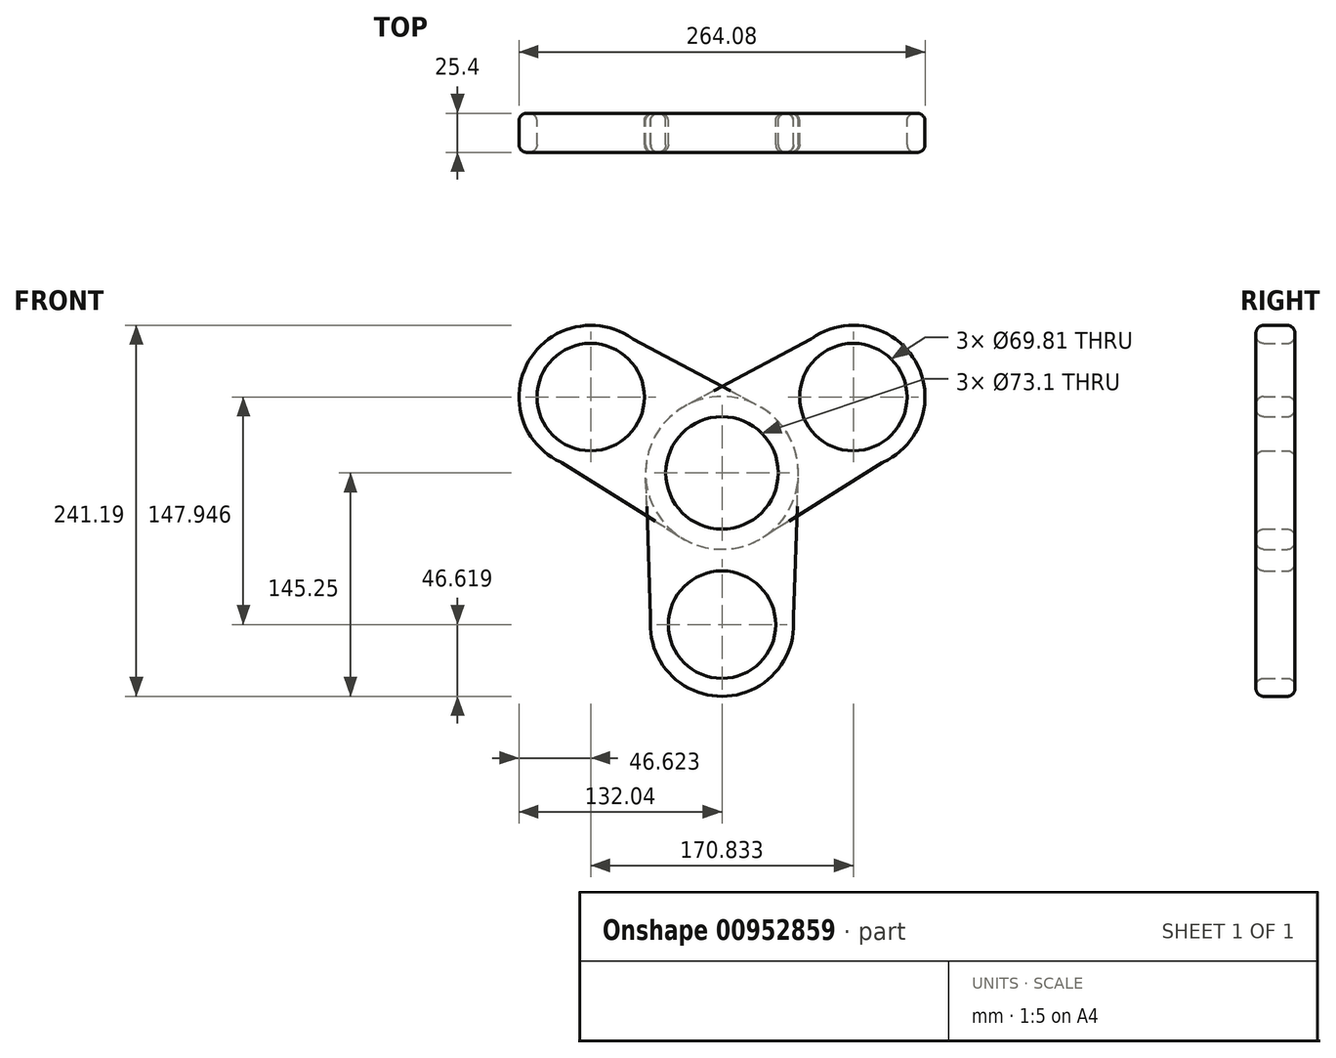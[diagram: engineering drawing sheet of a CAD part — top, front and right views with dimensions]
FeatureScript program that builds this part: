
annotation { "Feature Type Name" : "Feature", "Feature Type Description" : "" }
export const myFeature = defineFeature(function(context is Context, id is Id, definition is map)
    precondition{}
    {
        {
            var Q0;
            Q0=qCreatedBy(makeId("Front.planeOp"),FACE);
            var sketch = newSketch(context, id + "F0", { "sketchPlane" : qUnion([Q0])});
            skCircle(sketch, "E0", {"center": v(0, 0) * mm, "radius": 36.55 * mm});
            skCircle(sketch, "E1", {"center": v(0, 0) * mm, "radius": 49.65 * mm});
            skCircle(sketch, "E2", {"center": v(0, -98.63) * mm, "radius": 46.62 * mm});
            skLineSegment(sketch, "E3", {"start": v(46.38, -93.91) * mm, "end": v(49.68, 0) * mm});
            skLineSegment(sketch, "E4", {"start": v(-46.39, -93.95) * mm, "end": v(-49.68, 0) * mm});
            skCircle(sketch, "E5", {"center": v(0, -98.63) * mm, "radius": 34.9 * mm});
            skSolve(sketch);
        }
        {
            var Q0;
            Q0=makeQuery(id+"F0.imprint","IMPRINT",FACE,{"disambiguationData":[TD([[makeQuery(id+"F0.imprint","IMPRINT",EDGE,{"derivedFrom":sQuery(id+"F0.wireOp",EDGE,"E5")}),-1.0]])]});
            var Q1;
            Q1=makeQuery(id+"F0.imprint","IMPRINT",FACE,{"disambiguationData":[TD([[makeQuery(id+"F0.imprint","IMPRINT",EDGE,{"derivedFrom":sQuery(id+"F0.wireOp",EDGE,"E0")}),-1.0]])]});
            var Q2;
            {var subQ0=sQuery(id+"F0.wireOp",EDGE,"E3");var subQ1=sQuery(id+"F0.wireOp",EDGE,"E1");var subQ2=makeQuery(id+"F0.imprint","INTERSECT",VERTEX,{"derivedFrom":[subQ1,subQ0]});Q2=makeQuery(id+"F0.imprint","IMPRINT",FACE,{"disambiguationData":[TD([[makeQuery(id+"F0.imprint","IMPRINT",EDGE,{"disambiguationData":[TD([[subQ2,1.0]])],"derivedFrom":subQ1}),-1.0]])]});}
            extrude(context, id + "F1", {"entities" : qUnion([Q0, Q1, Q2]), "depth" : 25.4 * mm, "offsetDistance" : 25.4 * mm});
        }
        {
            var Q0;
            Q0=makeQuery(id+"F1.opExtrude","SWEPT_BODY",BODY,{"disambiguationData":[OSD([sQuery(id+"F0.wireOp",EDGE,"E0"),sQuery(id+"F0.wireOp",EDGE,"E1"),sQuery(id+"F0.wireOp",EDGE,"E2"),sQuery(id+"F0.wireOp",EDGE,"E3"),sQuery(id+"F0.wireOp",EDGE,"E4"),sQuery(id+"F0.wireOp",EDGE,"E5")])]});
            var Q1;
            Q1=makeQuery(id+"F1.opExtrude","CAP_EDGE",EDGE,{"disambiguationData":[OSD([sQuery(id+"F0.wireOp",EDGE,"E0")])],"isStart":false});
            circularPattern(context, id + "F2", {"entities" : qUnion([Q0]), "axis" : qUnion([Q1]), "angle" : 360 * degree, "instanceCount" : 3, "equalSpace" : true});
        }
        {
            var Q0;
            Q0=makeQuery(id+"F2.opPattern","COPY",EDGE,{"derivedFrom":makeQuery(id+"F1.opExtrude","CAP_EDGE",EDGE,{"disambiguationData":[OSD([sQuery(id+"F0.wireOp",EDGE,"E5")])],"isStart":true}),"instanceName":"2"});
            var Q1;
            Q1=makeQuery(id+"F2.opPattern","COPY",EDGE,{"derivedFrom":makeQuery(id+"F1.opExtrude","CAP_EDGE",EDGE,{"disambiguationData":[OSD([sQuery(id+"F0.wireOp",EDGE,"E2")])],"isStart":true}),"instanceName":"2"});
            var Q2;
            Q2=makeQuery(id+"F2.opPattern","COPY",EDGE,{"derivedFrom":makeQuery(id+"F1.opExtrude","CAP_EDGE",EDGE,{"disambiguationData":[OSD([sQuery(id+"F0.wireOp",EDGE,"E2")])],"isStart":false}),"instanceName":"2"});
            var Q3;
            Q3=makeQuery(id+"F2.opPattern","COPY",EDGE,{"derivedFrom":makeQuery(id+"F1.opExtrude","CAP_EDGE",EDGE,{"disambiguationData":[OSD([sQuery(id+"F0.wireOp",EDGE,"E4")])],"isStart":true}),"instanceName":"2"});
            var Q4;
            Q4=makeQuery(id+"F2.opPattern","COPY",EDGE,{"derivedFrom":makeQuery(id+"F1.opExtrude","CAP_EDGE",EDGE,{"disambiguationData":[OSD([sQuery(id+"F0.wireOp",EDGE,"E5")])],"isStart":true}),"instanceName":"1"});
            var Q5;
            Q5=makeQuery(id+"F1.opExtrude","SWEPT_FACE",FACE,{"disambiguationData":[OSD([sQuery(id+"F0.wireOp",EDGE,"E5")])]});
            var Q6;
            Q6=makeQuery(id+"F2.opPattern","COPY",FACE,{"derivedFrom":makeQuery(id+"F1.opExtrude","SWEPT_FACE",FACE,{"disambiguationData":[OSD([sQuery(id+"F0.wireOp",EDGE,"E1")])]}),"instanceName":"1"});
            var Q7;
            Q7=makeQuery(id+"F2.opPattern","COPY",EDGE,{"derivedFrom":makeQuery(id+"F1.opExtrude","SWEPT_EDGE",EDGE,{"disambiguationData":[OSD([sQuery(id+"F0.wireOp",EDGE,"E1"),sQuery(id+"F0.wireOp",EDGE,"E3")])]}),"instanceName":"2"});
            var Q8;
            Q8=makeQuery(id+"F1.opExtrude","SWEPT_EDGE",EDGE,{"disambiguationData":[OSD([sQuery(id+"F0.wireOp",EDGE,"E1"),sQuery(id+"F0.wireOp",EDGE,"E4")])]});
            var Q9;
            Q9=makeQuery(id+"F2.opPattern","COPY",EDGE,{"derivedFrom":makeQuery(id+"F1.opExtrude","CAP_EDGE",EDGE,{"disambiguationData":[OSD([sQuery(id+"F0.wireOp",EDGE,"E0")])],"isStart":true}),"instanceName":"1"});
            var Q10;
            Q10=makeQuery(id+"F1.opExtrude","SWEPT_FACE",FACE,{"disambiguationData":[OSD([sQuery(id+"F0.wireOp",EDGE,"E1")])]});
            var Q11;
            Q11=makeQuery(id+"F1.opExtrude","SWEPT_EDGE",EDGE,{"disambiguationData":[OSD([sQuery(id+"F0.wireOp",EDGE,"E2"),sQuery(id+"F0.wireOp",EDGE,"E3")])]});
            var Q12;
            Q12=makeQuery(id+"F2.opPattern","COPY",EDGE,{"derivedFrom":makeQuery(id+"F1.opExtrude","SWEPT_EDGE",EDGE,{"disambiguationData":[OSD([sQuery(id+"F0.wireOp",EDGE,"E2"),sQuery(id+"F0.wireOp",EDGE,"E4")])]}),"instanceName":"1"});
            var Q13;
            Q13=makeQuery(id+"F2.opPattern","COPY",EDGE,{"derivedFrom":makeQuery(id+"F1.opExtrude","SWEPT_EDGE",EDGE,{"disambiguationData":[OSD([sQuery(id+"F0.wireOp",EDGE,"E1"),sQuery(id+"F0.wireOp",EDGE,"E3")])]}),"instanceName":"1"});
            var Q14;
            Q14=makeQuery(id+"F1.opExtrude","CAP_EDGE",EDGE,{"disambiguationData":[OSD([sQuery(id+"F0.wireOp",EDGE,"E0")])],"isStart":true});
            var Q15;
            Q15=makeQuery(id+"F1.opExtrude","CAP_EDGE",EDGE,{"disambiguationData":[OSD([sQuery(id+"F0.wireOp",EDGE,"E0")])],"isStart":false});
            var Q16;
            Q16=makeQuery(id+"F1.opExtrude","CAP_EDGE",EDGE,{"disambiguationData":[OSD([sQuery(id+"F0.wireOp",EDGE,"E3")])],"isStart":true});
            var Q17;
            Q17=makeQuery(id+"F2.opPattern","COPY",FACE,{"derivedFrom":makeQuery(id+"F1.opExtrude","SWEPT_FACE",FACE,{"disambiguationData":[OSD([sQuery(id+"F0.wireOp",EDGE,"E4")])]}),"instanceName":"1"});
            var Q18;
            Q18=makeQuery(id+"F2.opPattern","COPY",EDGE,{"derivedFrom":makeQuery(id+"F1.opExtrude","CAP_EDGE",EDGE,{"disambiguationData":[OSD([sQuery(id+"F0.wireOp",EDGE,"E3")])],"isStart":true}),"instanceName":"1"});
            var Q19;
            Q19=makeQuery(id+"F1.opExtrude","CAP_EDGE",EDGE,{"disambiguationData":[OSD([sQuery(id+"F0.wireOp",EDGE,"E1")])],"isStart":false});
            var Q20;
            Q20=makeQuery(id+"F1.opExtrude","CAP_EDGE",EDGE,{"disambiguationData":[OSD([sQuery(id+"F0.wireOp",EDGE,"E2")])],"isStart":false});
            var Q21;
            Q21=makeQuery(id+"F2.opPattern","COPY",FACE,{"derivedFrom":makeQuery(id+"F1.opExtrude","CAP_FACE",FACE,{"disambiguationData":[OSD([sQuery(id+"F0.wireOp",EDGE,"E0"),sQuery(id+"F0.wireOp",EDGE,"E1"),sQuery(id+"F0.wireOp",EDGE,"E2"),sQuery(id+"F0.wireOp",EDGE,"E3"),sQuery(id+"F0.wireOp",EDGE,"E4"),sQuery(id+"F0.wireOp",EDGE,"E5")])],"isStart":true}),"instanceName":"1"});
            var Q22;
            Q22=makeQuery(id+"F1.opExtrude","CAP_FACE",FACE,{"disambiguationData":[OSD([sQuery(id+"F0.wireOp",EDGE,"E0"),sQuery(id+"F0.wireOp",EDGE,"E1"),sQuery(id+"F0.wireOp",EDGE,"E2"),sQuery(id+"F0.wireOp",EDGE,"E3"),sQuery(id+"F0.wireOp",EDGE,"E4"),sQuery(id+"F0.wireOp",EDGE,"E5")])],"isStart":false});
            var Q23;
            Q23=makeQuery(id+"F2.opPattern","COPY",EDGE,{"derivedFrom":makeQuery(id+"F1.opExtrude","CAP_EDGE",EDGE,{"disambiguationData":[OSD([sQuery(id+"F0.wireOp",EDGE,"E1")])],"isStart":true}),"instanceName":"1"});
            var Q24;
            Q24=makeQuery(id+"F1.opExtrude","CAP_EDGE",EDGE,{"disambiguationData":[OSD([sQuery(id+"F0.wireOp",EDGE,"E4")])],"isStart":true});
            var Q25;
            Q25=makeQuery(id+"F2.opPattern","COPY",EDGE,{"derivedFrom":makeQuery(id+"F1.opExtrude","CAP_EDGE",EDGE,{"disambiguationData":[OSD([sQuery(id+"F0.wireOp",EDGE,"E0")])],"isStart":false}),"instanceName":"2"});
            var Q26;
            Q26=makeQuery(id+"F2.opPattern","COPY",EDGE,{"derivedFrom":makeQuery(id+"F1.opExtrude","SWEPT_EDGE",EDGE,{"disambiguationData":[OSD([sQuery(id+"F0.wireOp",EDGE,"E1"),sQuery(id+"F0.wireOp",EDGE,"E4")])]}),"instanceName":"1"});
            var Q27;
            Q27=makeQuery(id+"F2.opPattern","COPY",EDGE,{"derivedFrom":makeQuery(id+"F1.opExtrude","CAP_EDGE",EDGE,{"disambiguationData":[OSD([sQuery(id+"F0.wireOp",EDGE,"E2")])],"isStart":true}),"instanceName":"1"});
            var Q28;
            Q28=makeQuery(id+"F2.opPattern","COPY",EDGE,{"derivedFrom":makeQuery(id+"F1.opExtrude","CAP_EDGE",EDGE,{"disambiguationData":[OSD([sQuery(id+"F0.wireOp",EDGE,"E3")])],"isStart":false}),"instanceName":"1"});
            var Q29;
            Q29=makeQuery(id+"F1.opExtrude","SWEPT_FACE",FACE,{"disambiguationData":[OSD([sQuery(id+"F0.wireOp",EDGE,"E2")])]});
            var Q30;
            Q30=makeQuery(id+"F2.opPattern","COPY",FACE,{"derivedFrom":makeQuery(id+"F1.opExtrude","SWEPT_FACE",FACE,{"disambiguationData":[OSD([sQuery(id+"F0.wireOp",EDGE,"E0")])]}),"instanceName":"1"});
            var Q31;
            Q31=makeQuery(id+"F2.opPattern","COPY",EDGE,{"derivedFrom":makeQuery(id+"F1.opExtrude","CAP_EDGE",EDGE,{"disambiguationData":[OSD([sQuery(id+"F0.wireOp",EDGE,"E1")])],"isStart":false}),"instanceName":"2"});
            var Q32;
            Q32=makeQuery(id+"F2.opPattern","COPY",EDGE,{"derivedFrom":makeQuery(id+"F1.opExtrude","SWEPT_EDGE",EDGE,{"disambiguationData":[OSD([sQuery(id+"F0.wireOp",EDGE,"E2"),sQuery(id+"F0.wireOp",EDGE,"E3")])]}),"instanceName":"1"});
            var Q33;
            Q33=makeQuery(id+"F2.opPattern","COPY",EDGE,{"derivedFrom":makeQuery(id+"F1.opExtrude","CAP_EDGE",EDGE,{"disambiguationData":[OSD([sQuery(id+"F0.wireOp",EDGE,"E5")])],"isStart":false}),"instanceName":"2"});
            var Q34;
            Q34=makeQuery(id+"F2.opPattern","COPY",EDGE,{"derivedFrom":makeQuery(id+"F1.opExtrude","SWEPT_EDGE",EDGE,{"disambiguationData":[OSD([sQuery(id+"F0.wireOp",EDGE,"E2"),sQuery(id+"F0.wireOp",EDGE,"E3")])]}),"instanceName":"2"});
            var Q35;
            Q35=makeQuery(id+"F2.opPattern","COPY",EDGE,{"derivedFrom":makeQuery(id+"F1.opExtrude","CAP_EDGE",EDGE,{"disambiguationData":[OSD([sQuery(id+"F0.wireOp",EDGE,"E5")])],"isStart":false}),"instanceName":"1"});
            var Q36;
            Q36=makeQuery(id+"F2.opPattern","COPY",EDGE,{"derivedFrom":makeQuery(id+"F1.opExtrude","CAP_EDGE",EDGE,{"disambiguationData":[OSD([sQuery(id+"F0.wireOp",EDGE,"E1")])],"isStart":false}),"instanceName":"1"});
            var Q37;
            Q37=makeQuery(id+"F2.opPattern","COPY",FACE,{"derivedFrom":makeQuery(id+"F1.opExtrude","SWEPT_FACE",FACE,{"disambiguationData":[OSD([sQuery(id+"F0.wireOp",EDGE,"E4")])]}),"instanceName":"2"});
            var Q38;
            Q38=makeQuery(id+"F1.opExtrude","CAP_EDGE",EDGE,{"disambiguationData":[OSD([sQuery(id+"F0.wireOp",EDGE,"E5")])],"isStart":false});
            var Q39;
            Q39=makeQuery(id+"F2.opPattern","COPY",FACE,{"derivedFrom":makeQuery(id+"F1.opExtrude","SWEPT_FACE",FACE,{"disambiguationData":[OSD([sQuery(id+"F0.wireOp",EDGE,"E2")])]}),"instanceName":"1"});
            var Q40;
            Q40=makeQuery(id+"F1.opExtrude","CAP_EDGE",EDGE,{"disambiguationData":[OSD([sQuery(id+"F0.wireOp",EDGE,"E1")])],"isStart":true});
            var Q41;
            Q41=makeQuery(id+"F2.opPattern","COPY",FACE,{"derivedFrom":makeQuery(id+"F1.opExtrude","SWEPT_FACE",FACE,{"disambiguationData":[OSD([sQuery(id+"F0.wireOp",EDGE,"E2")])]}),"instanceName":"2"});
            var Q42;
            Q42=makeQuery(id+"F1.opExtrude","CAP_EDGE",EDGE,{"disambiguationData":[OSD([sQuery(id+"F0.wireOp",EDGE,"E2")])],"isStart":true});
            var Q43;
            Q43=makeQuery(id+"F2.opPattern","COPY",EDGE,{"derivedFrom":makeQuery(id+"F1.opExtrude","SWEPT_EDGE",EDGE,{"disambiguationData":[OSD([sQuery(id+"F0.wireOp",EDGE,"E1"),sQuery(id+"F0.wireOp",EDGE,"E4")])]}),"instanceName":"2"});
            var Q44;
            Q44=makeQuery(id+"F2.opPattern","COPY",FACE,{"derivedFrom":makeQuery(id+"F1.opExtrude","SWEPT_FACE",FACE,{"disambiguationData":[OSD([sQuery(id+"F0.wireOp",EDGE,"E5")])]}),"instanceName":"2"});
            var Q45;
            Q45=makeQuery(id+"F1.opExtrude","CAP_EDGE",EDGE,{"disambiguationData":[OSD([sQuery(id+"F0.wireOp",EDGE,"E4")])],"isStart":false});
            var Q46;
            Q46=makeQuery(id+"F1.opExtrude","CAP_EDGE",EDGE,{"disambiguationData":[OSD([sQuery(id+"F0.wireOp",EDGE,"E5")])],"isStart":true});
            var Q47;
            Q47=makeQuery(id+"F2.opPattern","COPY",EDGE,{"derivedFrom":makeQuery(id+"F1.opExtrude","SWEPT_EDGE",EDGE,{"disambiguationData":[OSD([sQuery(id+"F0.wireOp",EDGE,"E2"),sQuery(id+"F0.wireOp",EDGE,"E4")])]}),"instanceName":"2"});
            var Q48;
            Q48=makeQuery(id+"F2.opPattern","COPY",FACE,{"derivedFrom":makeQuery(id+"F1.opExtrude","CAP_FACE",FACE,{"disambiguationData":[OSD([sQuery(id+"F0.wireOp",EDGE,"E0"),sQuery(id+"F0.wireOp",EDGE,"E1"),sQuery(id+"F0.wireOp",EDGE,"E2"),sQuery(id+"F0.wireOp",EDGE,"E3"),sQuery(id+"F0.wireOp",EDGE,"E4"),sQuery(id+"F0.wireOp",EDGE,"E5")])],"isStart":true}),"instanceName":"2"});
            var Q49;
            Q49=makeQuery(id+"F1.opExtrude","SWEPT_FACE",FACE,{"disambiguationData":[OSD([sQuery(id+"F0.wireOp",EDGE,"E3")])]});
            var Q50;
            Q50=makeQuery(id+"F2.opPattern","COPY",EDGE,{"derivedFrom":makeQuery(id+"F1.opExtrude","CAP_EDGE",EDGE,{"disambiguationData":[OSD([sQuery(id+"F0.wireOp",EDGE,"E1")])],"isStart":true}),"instanceName":"2"});
            var Q51;
            Q51=makeQuery(id+"F2.opPattern","COPY",FACE,{"derivedFrom":makeQuery(id+"F1.opExtrude","SWEPT_FACE",FACE,{"disambiguationData":[OSD([sQuery(id+"F0.wireOp",EDGE,"E0")])]}),"instanceName":"2"});
            var Q52;
            Q52=makeQuery(id+"F2.opPattern","COPY",EDGE,{"derivedFrom":makeQuery(id+"F1.opExtrude","CAP_EDGE",EDGE,{"disambiguationData":[OSD([sQuery(id+"F0.wireOp",EDGE,"E2")])],"isStart":false}),"instanceName":"1"});
            var Q53;
            Q53=makeQuery(id+"F2.opPattern","COPY",FACE,{"derivedFrom":makeQuery(id+"F1.opExtrude","SWEPT_FACE",FACE,{"disambiguationData":[OSD([sQuery(id+"F0.wireOp",EDGE,"E5")])]}),"instanceName":"1"});
            var Q54;
            Q54=makeQuery(id+"F1.opExtrude","CAP_FACE",FACE,{"disambiguationData":[OSD([sQuery(id+"F0.wireOp",EDGE,"E0"),sQuery(id+"F0.wireOp",EDGE,"E1"),sQuery(id+"F0.wireOp",EDGE,"E2"),sQuery(id+"F0.wireOp",EDGE,"E3"),sQuery(id+"F0.wireOp",EDGE,"E4"),sQuery(id+"F0.wireOp",EDGE,"E5")])],"isStart":true});
            var Q55;
            Q55=makeQuery(id+"F2.opPattern","COPY",FACE,{"derivedFrom":makeQuery(id+"F1.opExtrude","CAP_FACE",FACE,{"disambiguationData":[OSD([sQuery(id+"F0.wireOp",EDGE,"E0"),sQuery(id+"F0.wireOp",EDGE,"E1"),sQuery(id+"F0.wireOp",EDGE,"E2"),sQuery(id+"F0.wireOp",EDGE,"E3"),sQuery(id+"F0.wireOp",EDGE,"E4"),sQuery(id+"F0.wireOp",EDGE,"E5")])],"isStart":false}),"instanceName":"1"});
            var Q56;
            Q56=makeQuery(id+"F2.opPattern","COPY",FACE,{"derivedFrom":makeQuery(id+"F1.opExtrude","CAP_FACE",FACE,{"disambiguationData":[OSD([sQuery(id+"F0.wireOp",EDGE,"E0"),sQuery(id+"F0.wireOp",EDGE,"E1"),sQuery(id+"F0.wireOp",EDGE,"E2"),sQuery(id+"F0.wireOp",EDGE,"E3"),sQuery(id+"F0.wireOp",EDGE,"E4"),sQuery(id+"F0.wireOp",EDGE,"E5")])],"isStart":false}),"instanceName":"2"});
            var Q57;
            Q57=makeQuery(id+"F2.opPattern","COPY",EDGE,{"derivedFrom":makeQuery(id+"F1.opExtrude","CAP_EDGE",EDGE,{"disambiguationData":[OSD([sQuery(id+"F0.wireOp",EDGE,"E0")])],"isStart":false}),"instanceName":"1"});
            var Q58;
            Q58=makeQuery(id+"F2.opPattern","COPY",FACE,{"derivedFrom":makeQuery(id+"F1.opExtrude","SWEPT_FACE",FACE,{"disambiguationData":[OSD([sQuery(id+"F0.wireOp",EDGE,"E1")])]}),"instanceName":"2"});
            var Q59;
            Q59=makeQuery(id+"F1.opExtrude","SWEPT_EDGE",EDGE,{"disambiguationData":[OSD([sQuery(id+"F0.wireOp",EDGE,"E2"),sQuery(id+"F0.wireOp",EDGE,"E4")])]});
            var Q60;
            Q60=makeQuery(id+"F2.opPattern","COPY",EDGE,{"derivedFrom":makeQuery(id+"F1.opExtrude","CAP_EDGE",EDGE,{"disambiguationData":[OSD([sQuery(id+"F0.wireOp",EDGE,"E3")])],"isStart":true}),"instanceName":"2"});
            var Q61;
            Q61=makeQuery(id+"F2.opPattern","COPY",EDGE,{"derivedFrom":makeQuery(id+"F1.opExtrude","CAP_EDGE",EDGE,{"disambiguationData":[OSD([sQuery(id+"F0.wireOp",EDGE,"E4")])],"isStart":false}),"instanceName":"1"});
            var Q62;
            Q62=makeQuery(id+"F2.opPattern","COPY",EDGE,{"derivedFrom":makeQuery(id+"F1.opExtrude","CAP_EDGE",EDGE,{"disambiguationData":[OSD([sQuery(id+"F0.wireOp",EDGE,"E3")])],"isStart":false}),"instanceName":"2"});
            var Q63;
            Q63=makeQuery(id+"F1.opExtrude","CAP_EDGE",EDGE,{"disambiguationData":[OSD([sQuery(id+"F0.wireOp",EDGE,"E3")])],"isStart":false});
            var Q64;
            Q64=makeQuery(id+"F2.opPattern","COPY",EDGE,{"derivedFrom":makeQuery(id+"F1.opExtrude","CAP_EDGE",EDGE,{"disambiguationData":[OSD([sQuery(id+"F0.wireOp",EDGE,"E4")])],"isStart":true}),"instanceName":"1"});
            var Q65;
            Q65=makeQuery(id+"F1.opExtrude","SWEPT_FACE",FACE,{"disambiguationData":[OSD([sQuery(id+"F0.wireOp",EDGE,"E0")])]});
            var Q66;
            Q66=makeQuery(id+"F2.opPattern","COPY",EDGE,{"derivedFrom":makeQuery(id+"F1.opExtrude","CAP_EDGE",EDGE,{"disambiguationData":[OSD([sQuery(id+"F0.wireOp",EDGE,"E4")])],"isStart":false}),"instanceName":"2"});
            var Q67;
            Q67=makeQuery(id+"F2.opPattern","COPY",FACE,{"derivedFrom":makeQuery(id+"F1.opExtrude","SWEPT_FACE",FACE,{"disambiguationData":[OSD([sQuery(id+"F0.wireOp",EDGE,"E3")])]}),"instanceName":"2"});
            var Q68;
            Q68=makeQuery(id+"F2.opPattern","COPY",EDGE,{"derivedFrom":makeQuery(id+"F1.opExtrude","CAP_EDGE",EDGE,{"disambiguationData":[OSD([sQuery(id+"F0.wireOp",EDGE,"E0")])],"isStart":true}),"instanceName":"2"});
            var Q69;
            Q69=makeQuery(id+"F1.opExtrude","SWEPT_EDGE",EDGE,{"disambiguationData":[OSD([sQuery(id+"F0.wireOp",EDGE,"E1"),sQuery(id+"F0.wireOp",EDGE,"E3")])]});
            var Q70;
            Q70=makeQuery(id+"F1.opExtrude","SWEPT_FACE",FACE,{"disambiguationData":[OSD([sQuery(id+"F0.wireOp",EDGE,"E4")])]});
            var Q71;
            Q71=makeQuery(id+"F2.opPattern","COPY",FACE,{"derivedFrom":makeQuery(id+"F1.opExtrude","SWEPT_FACE",FACE,{"disambiguationData":[OSD([sQuery(id+"F0.wireOp",EDGE,"E3")])]}),"instanceName":"1"});
            fillet(context, id + "F3", {"entities" : qUnion([Q0, Q1, Q2, Q3, Q4, Q5, Q6, Q7, Q8, Q9, Q10, Q11, Q12, Q13, Q14, Q15, Q16, Q17, Q18, Q19, Q20, Q21, Q22, Q23, Q24, Q25, Q26, Q27, Q28, Q29, Q30, Q31, Q32, Q33, Q34, Q35, Q36, Q37, Q38, Q39, Q40, Q41, Q42, Q43, Q44, Q45, Q46, Q47, Q48, Q49, Q50, Q51, Q52, Q53, Q54, Q55, Q56, Q57, Q58, Q59, Q60, Q61, Q62, Q63, Q64, Q65, Q66, Q67, Q68, Q69, Q70, Q71]), "radius" : 5.08 * mm, "tangentPropagation" : true, "allowEdgeOverflow" : false});
        }
    });
